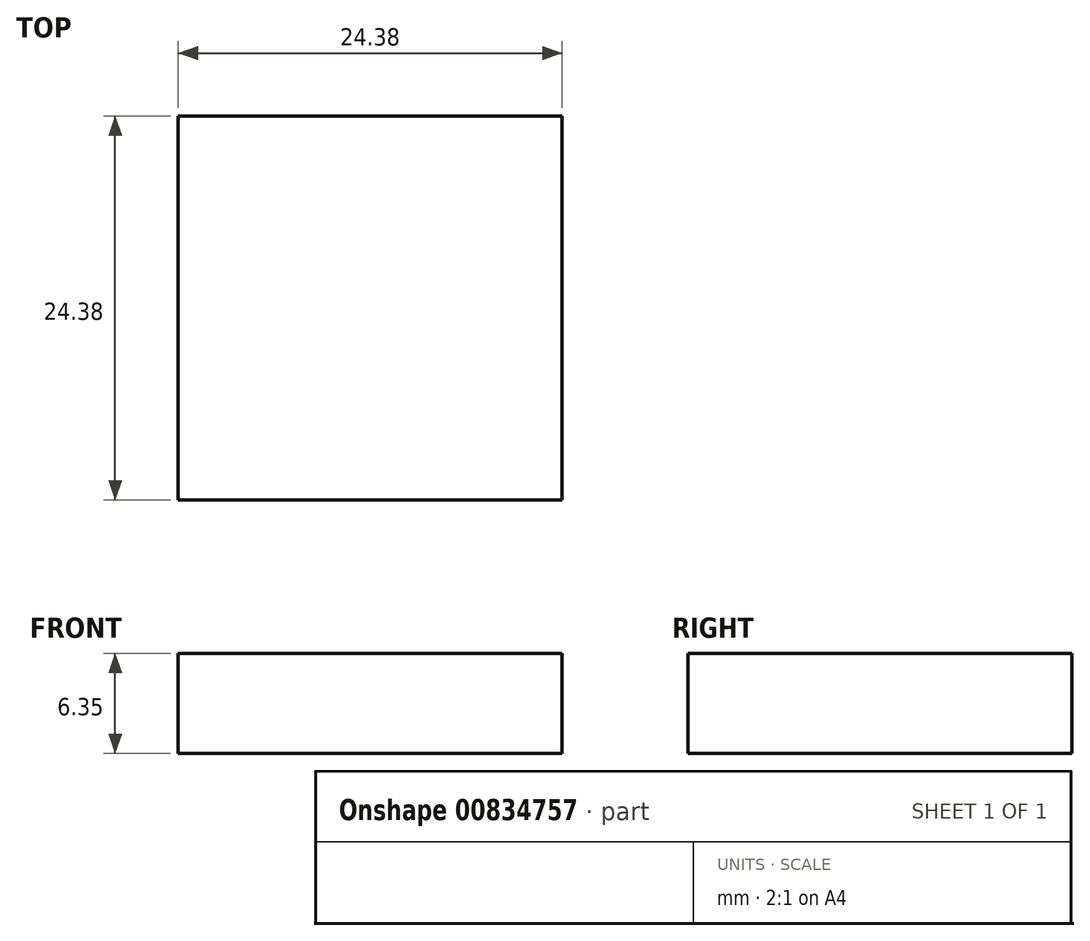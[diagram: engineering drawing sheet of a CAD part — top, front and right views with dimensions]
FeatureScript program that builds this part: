
annotation { "Feature Type Name" : "Feature", "Feature Type Description" : "" }
export const myFeature = defineFeature(function(context is Context, id is Id, definition is map)
    precondition{}
    {
        {
            var Q0;
            Q0=qCreatedBy(makeId("Top.planeOp"),FACE);
            var sketch = newSketch(context, id + "F0", { "sketchPlane" : qUnion([Q0])});
            skLineSegment(sketch, "E0.bottom", {"start": v(-1.52, -1.52) * mm, "end": v(22.86, -1.52) * mm});
            skLineSegment(sketch, "E0.top", {"start": v(-1.52, 22.86) * mm, "end": v(22.86, 22.86) * mm});
            skLineSegment(sketch, "E0.left", {"start": v(-1.52, -1.52) * mm, "end": v(-1.52, 22.86) * mm});
            skLineSegment(sketch, "E0.right", {"start": v(22.86, -1.52) * mm, "end": v(22.86, 22.86) * mm});
            skSolve(sketch);
        }
        {
            var Q0;
            Q0 = qSketchRegion(id + "F0", true);
            extrude(context, id + "F1", {"entities" : qUnion([Q0]), "depth" : 6.35 * mm, "offsetDistance" : 25.4 * mm});
        }
    });
